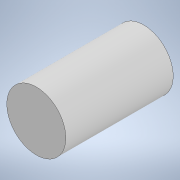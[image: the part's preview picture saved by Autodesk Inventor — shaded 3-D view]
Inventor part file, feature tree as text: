
AUTODESK INVENTOR PART (.ipt)
format: ipt  version: 2021 (Build 250183000, 183)  size: 88,064 bytes
history: native  units: mm
features: extrude x1, sketch x1
ambient origin geometry x8: Origin, YZ Plane, XZ Plane, XY Plane, X Axis, Y Axis, Z Axis, Center Point
bodies: Solid1 (feature_tree)
feature tree (2):
  extrude  "Extrusion1"  Depth=20.0mm TaperAngle=0.0deg
  sketch  "Sketch1"  dims[d0=11.0mm d1=20.0mm d2=0.0mm]
